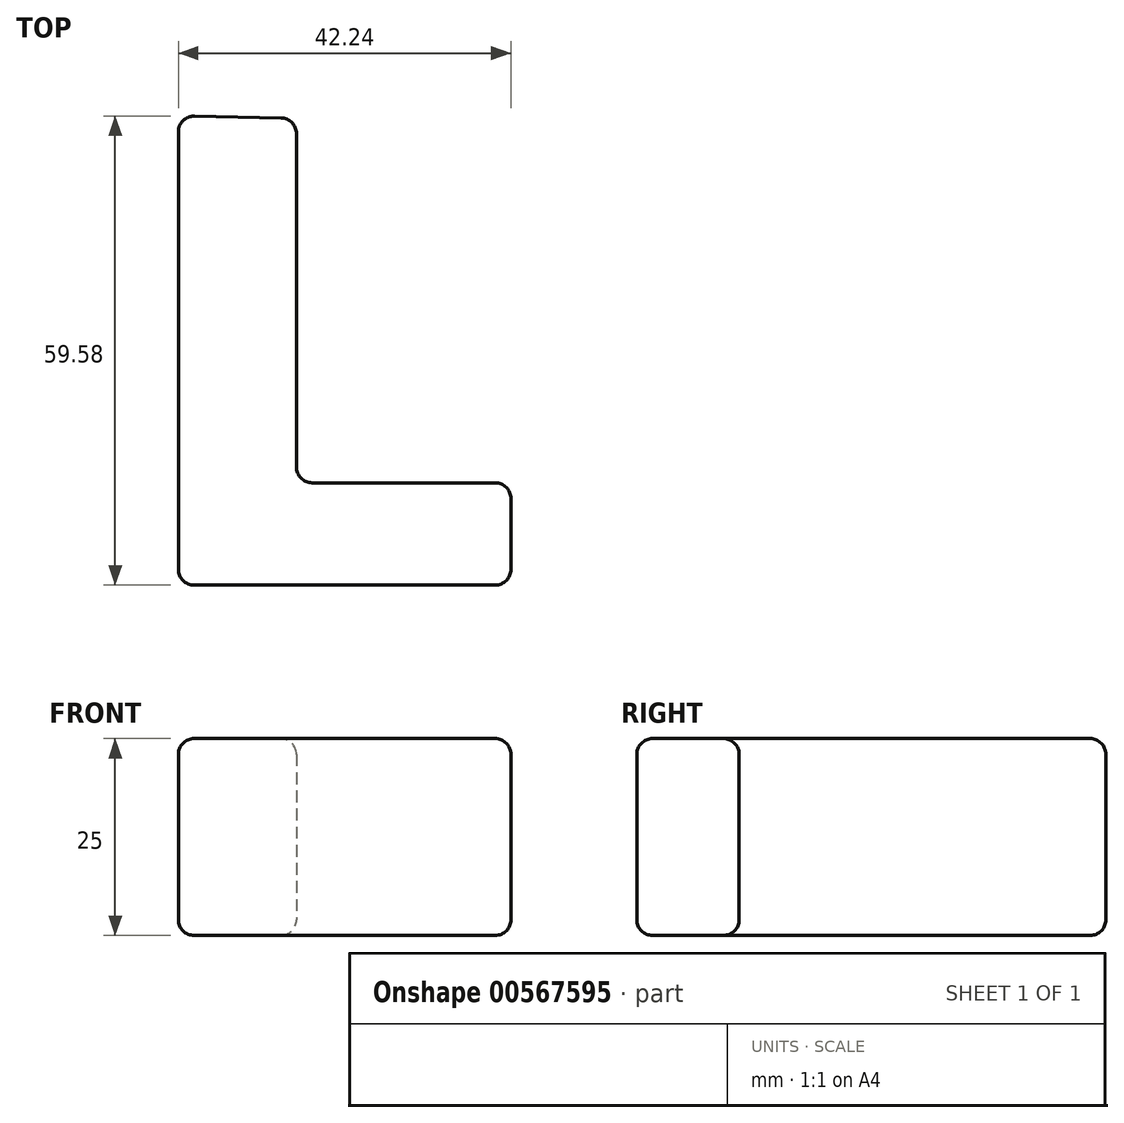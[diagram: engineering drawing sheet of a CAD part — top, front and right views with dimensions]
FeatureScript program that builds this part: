
annotation { "Feature Type Name" : "Feature", "Feature Type Description" : "" }
export const myFeature = defineFeature(function(context is Context, id is Id, definition is map)
    precondition{}
    {
        {
            var Q0;
            Q0=qCreatedBy(makeId("Top.planeOp"),FACE);
            var sketch = newSketch(context, id + "F0", { "sketchPlane" : qUnion([Q0])});
            skLineSegment(sketch, "E0", {"start": v(-28.28, 59.62) * mm, "end": v(-28.28, 0) * mm});
            skLineSegment(sketch, "E1", {"start": v(-28.28, 0) * mm, "end": v(13.96, 0) * mm});
            skLineSegment(sketch, "E2", {"start": v(13.96, 0) * mm, "end": v(13.96, 13) * mm});
            skLineSegment(sketch, "E3", {"start": v(13.96, 13) * mm, "end": v(-13.28, 13) * mm});
            skLineSegment(sketch, "E4", {"start": v(-13.28, 13) * mm, "end": v(-13.28, 59.31) * mm});
            skLineSegment(sketch, "E5", {"start": v(-13.28, 59.31) * mm, "end": v(-28.28, 59.62) * mm});
            skSolve(sketch);
        }
        {
            var Q0;
            Q0 = qSketchRegion(id + "F0", true);
            extrude(context, id + "F1", {"entities" : qUnion([Q0]), "depth" : 25 * mm, "offsetDistance" : 25 * mm});
        }
        {
            var Q0;
            Q0=makeQuery(id+"F1.opExtrude","CAP_FACE",FACE,{"disambiguationData":[OSD([sQuery(id+"F0.wireOp",EDGE,"E0"),sQuery(id+"F0.wireOp",EDGE,"E1"),sQuery(id+"F0.wireOp",EDGE,"E2"),sQuery(id+"F0.wireOp",EDGE,"E3"),sQuery(id+"F0.wireOp",EDGE,"E4"),sQuery(id+"F0.wireOp",EDGE,"E5")])],"isStart":false});
            var Q1;
            Q1=makeQuery(id+"F1.opExtrude","SWEPT_FACE",FACE,{"disambiguationData":[OSD([sQuery(id+"F0.wireOp",EDGE,"E4")])]});
            var Q2;
            Q2=makeQuery(id+"F1.opExtrude","SWEPT_FACE",FACE,{"disambiguationData":[OSD([sQuery(id+"F0.wireOp",EDGE,"E2")])]});
            var Q3;
            Q3=makeQuery(id+"F1.opExtrude","CAP_FACE",FACE,{"disambiguationData":[OSD([sQuery(id+"F0.wireOp",EDGE,"E0"),sQuery(id+"F0.wireOp",EDGE,"E1"),sQuery(id+"F0.wireOp",EDGE,"E2"),sQuery(id+"F0.wireOp",EDGE,"E3"),sQuery(id+"F0.wireOp",EDGE,"E4"),sQuery(id+"F0.wireOp",EDGE,"E5")])],"isStart":true});
            var Q4;
            Q4=makeQuery(id+"F1.opExtrude","SWEPT_FACE",FACE,{"disambiguationData":[OSD([sQuery(id+"F0.wireOp",EDGE,"E0")])]});
            var Q5;
            Q5=makeQuery(id+"F1.opExtrude","CAP_EDGE",EDGE,{"disambiguationData":[OSD([sQuery(id+"F0.wireOp",EDGE,"E1")])],"isStart":true});
            var Q6;
            Q6=makeQuery(id+"F1.opExtrude","CAP_EDGE",EDGE,{"disambiguationData":[OSD([sQuery(id+"F0.wireOp",EDGE,"E0")])],"isStart":true});
            var Q7;
            Q7=makeQuery(id+"F1.opExtrude","SWEPT_EDGE",EDGE,{"disambiguationData":[OSD([sQuery(id+"F0.wireOp",EDGE,"E0"),sQuery(id+"F0.wireOp",EDGE,"E1")])]});
            var Q8;
            Q8=makeQuery(id+"F1.opExtrude","SWEPT_EDGE",EDGE,{"disambiguationData":[OSD([sQuery(id+"F0.wireOp",EDGE,"E1"),sQuery(id+"F0.wireOp",EDGE,"E2")])]});
            var Q9;
            Q9=makeQuery(id+"F1.opExtrude","SWEPT_FACE",FACE,{"disambiguationData":[OSD([sQuery(id+"F0.wireOp",EDGE,"E1")])]});
            fillet(context, id + "F2", {"entities" : qUnion([Q0, Q1, Q2, Q3, Q4, Q5, Q6, Q7, Q8, Q9]), "radius" : 2 * mm, "tangentPropagation" : true, "allowEdgeOverflow" : false});
        }
    });
